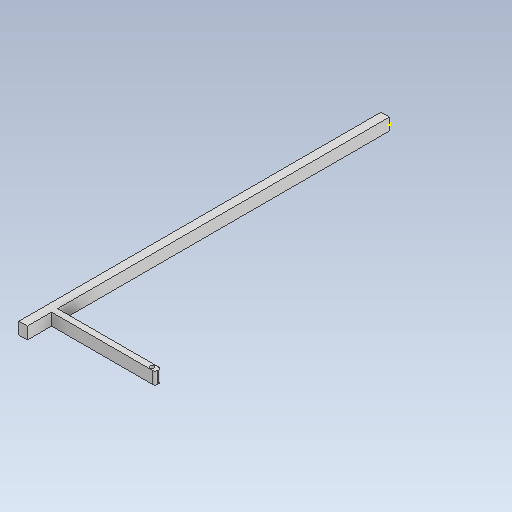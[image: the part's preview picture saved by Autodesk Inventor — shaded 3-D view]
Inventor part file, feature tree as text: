
AUTODESK INVENTOR PART (.ipt)
format: ipt  version: 2021 (Build 250183000, 183)  size: 124,416 bytes
history: native  units: mm
features: sketch x4, extrude x3, fillet x1
ambient origin geometry x8: Origin, YZ Plane, XZ Plane, XY Plane, X Axis, Y Axis, Z Axis, Center Point
bodies: Solid1 (feature_tree)
feature tree (8):
  extrude  "Extrusion1"  Depth=10.0mm
  sketch  "Sketch2"  dims[d2=300.0mm d3=0.0mm d4=5.0mm]
  extrude  "Extrusion2"  Depth=5.0mm
  extrude  "Extrusion3"  Depth=85.85mm
  fillet  "Fillet1"  Radius=2.5mm
  sketch  "Sketch1"  dims[d0=7.0mm d1=10.0mm]
  sketch  "Sketch3"  dims[d5=85.85mm d6=0.0mm d7=3.28mm d8=2.5mm]
  sketch  "Sketch4"  dims[d9=0.0mm d10=0.0mm d11=2.0mm d12=20.0mm]
